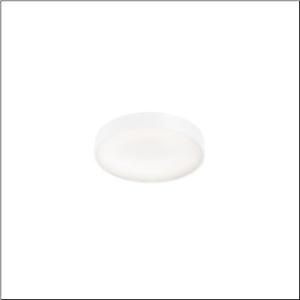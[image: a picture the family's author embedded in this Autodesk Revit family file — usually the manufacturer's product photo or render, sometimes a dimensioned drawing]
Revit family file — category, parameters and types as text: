
# Revit family: round_21_s_51mr34nd0321w
name_source: partatom
category: Lighting Fixtures
units: mm (PartAtom-declared; Revit-internal decimal feet)

## family parameters
Cut with Voids When Loaded = No
Host = Face
Light Source = No
Part Type = Normal
Room Calculation Point = No
Round Connector Dimension = Use Diameter
Shared = No

## types (1)
- Round 21 S (1 x LED, 3660 lm, 28.3 W, 3000K)
    Apparent Load = 28 VA
    CIE Flux Codes = 66 90 98 71 100
    Color Rendering = 80
    Color Temperature = 3000K
    Default Elevation = 1800 mm
    Description = Round 21 S, wall and ceiling luminaire, primary optical cover: micro prismatic cover, of PMMA, transparent, CAT 2 (L<= 3000cd/m²), light emission: direct/indirect distribution, primary light characteristic: symmetric, installation type: suspended mounting, surface-mounted, LED, rated luminous flux: 3.660lm, luminous efficacy: 129lm/W, light colour: 830, colour temperature: 3000K, control gear: DALI 2, with terminal, 5-pole, mains connection: 230V, AC, 50/60Hz, rated input power: 28.3W, housing, of aluminium, coated, white, diameter: 400mm, height: 62mm, protection rating (complete): IP40, insulation class (complete): insulation class I (protective earthing), certification: CE, impact resistance: IK04, permissible operating ambient temperature: -10..+35°C, packaging unit: 1 piece
    Height = 87 mm
    Lamp = 1 x LED
    Lamp Light Flux = 3660 lm
    Lamp Power = 28.3 W
    Lamp count = 1
    Length = 400 mm
    Luminous efficacy = 129 lm/W
    Manufacturer = Siteco
    ModVariant = No
    Model = 51MR34ND0321W
    Mounting Place = Wall
    Mounting Type = Surface mounted
    Number of Poles = 1
    OnlyDefault = Yes
    Power Factor = 1
    Product Name = Round 21 S
    Product group = wall and ceiling luminaire
    ProductGroupID = 2001
    Protection Class = Protection class I
    Protection Degree = IP 40
    RLX_Detail_Level = 1
    RLX_Emergency_Light_Flux = 0 lm
    RLX_Emergency_Type = 0
    RLX_Emergency_Type_DB = No
    RlxData = <blob elided: 12841 chars, md5=d034173e>
    Socket = socket
    Standby Power = 0 W
    System Light Flux = 3660 lm
    System Power = 28 W
    Type Comments = Product without accessories
    Type Image = l_1258334.jpg
    URL = http://relux.com
    VarID = ---
    Voltage = 0 V
    Weight = 0.00 kg
    Width = 0 mm  [stored 0 ft]

note: [stored X ft] marks values corroborated as IEEE doubles in the binary element streams (Revit-internal decimal feet)

## geometry (parser evidence)
native form markers: Sweep x10
no freeform markers — native parametric forms only
